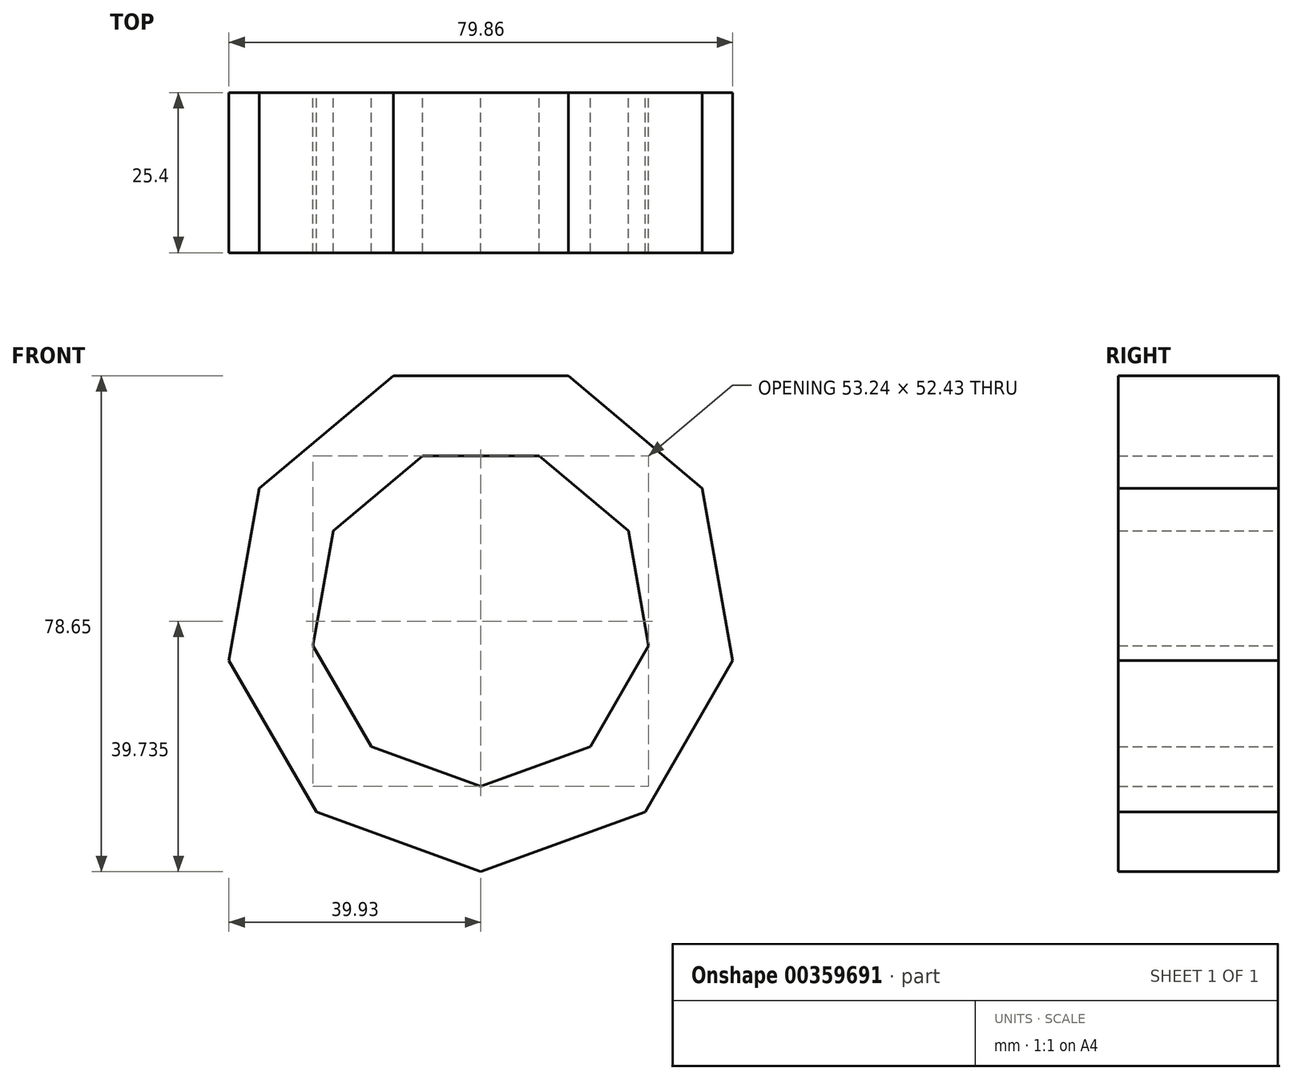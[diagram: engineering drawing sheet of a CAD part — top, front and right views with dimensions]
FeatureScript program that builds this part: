
annotation { "Feature Type Name" : "Feature", "Feature Type Description" : "" }
export const myFeature = defineFeature(function(context is Context, id is Id, definition is map)
    precondition{}
    {
        {
            var Q0;
            Q0=qCreatedBy(makeId("Front.planeOp"),FACE);
            var sketch = newSketch(context, id + "F0", { "sketchPlane" : qUnion([Q0])});
            skLineSegment(sketch, "E0", {"start": v(0, 0) * mm, "end": v(0, 38.1) * mm});
            skCircle(sketch, "E1.cCircle", {"center": v(0, 0) * mm, "radius": 38.1 * mm, "construction": true});
            skLineSegment(sketch, "E1.0", {"start": v(-13.87, 38.1) * mm, "end": v(13.87, 38.1) * mm});
            skLineSegment(sketch, "E1.1", {"start": v(13.87, 38.1) * mm, "end": v(35.11, 20.27) * mm});
            skLineSegment(sketch, "E1.2", {"start": v(35.11, 20.27) * mm, "end": v(39.93, -7.04) * mm});
            skLineSegment(sketch, "E1.3", {"start": v(39.93, -7.04) * mm, "end": v(26.06, -31.06) * mm});
            skLineSegment(sketch, "E1.4", {"start": v(26.06, -31.06) * mm, "end": v(0, -40.55) * mm});
            skLineSegment(sketch, "E1.5", {"start": v(0, -40.55) * mm, "end": v(-26.06, -31.06) * mm});
            skLineSegment(sketch, "E1.6", {"start": v(-26.06, -31.06) * mm, "end": v(-39.93, -7.04) * mm});
            skLineSegment(sketch, "E1.7", {"start": v(-39.93, -7.04) * mm, "end": v(-35.11, 20.27) * mm});
            skLineSegment(sketch, "E1.8", {"start": v(-35.11, 20.27) * mm, "end": v(-13.87, 38.1) * mm});
            skPoint(sketch, "E1.0.midPoint", {"position": v(0, 38.1) * mm});
            skPoint(sketch, "E2.0.midPoint", {"position": v(0, 25.4) * mm});
            skPoint(sketch, "E2.0.start.orphan", {"position": v(-9.24, 25.4) * mm});
            skPoint(sketch, "E2.1.start.orphan", {"position": v(9.24, 25.4) * mm});
            skLineSegment(sketch, "E3", {"start": v(0, 0) * mm, "end": v(0, 19.05) * mm});
            skLineSegment(sketch, "E4", {"start": v(0, 0) * mm, "end": v(0, 25.4) * mm});
            skCircle(sketch, "E5.cCircle", {"center": v(0, 0) * mm, "radius": 25.4 * mm, "construction": true});
            skLineSegment(sketch, "E5.0", {"start": v(-9.24, 25.4) * mm, "end": v(9.24, 25.4) * mm});
            skLineSegment(sketch, "E5.1", {"start": v(9.24, 25.4) * mm, "end": v(23.4, 13.52) * mm});
            skLineSegment(sketch, "E5.2", {"start": v(23.4, 13.52) * mm, "end": v(26.62, -4.7) * mm});
            skLineSegment(sketch, "E5.3", {"start": v(26.62, -4.7) * mm, "end": v(17.37, -20.7) * mm});
            skLineSegment(sketch, "E5.4", {"start": v(17.37, -20.7) * mm, "end": v(0, -27.03) * mm});
            skLineSegment(sketch, "E5.5", {"start": v(0, -27.03) * mm, "end": v(-17.37, -20.7) * mm});
            skLineSegment(sketch, "E5.6", {"start": v(-17.37, -20.7) * mm, "end": v(-26.62, -4.7) * mm});
            skLineSegment(sketch, "E5.7", {"start": v(-26.62, -4.7) * mm, "end": v(-23.4, 13.52) * mm});
            skLineSegment(sketch, "E5.8", {"start": v(-23.4, 13.52) * mm, "end": v(-9.24, 25.4) * mm});
            skSolve(sketch);
        }
        {
            var Q0;
            {var subQ3=sQuery(id+"F0.wireOp",EDGE,"E1.1");Q0=makeQuery(id+"F0.imprint","IMPRINT",FACE,{"disambiguationData":[TD([[makeQuery(id+"F0.imprint","IMPRINT",EDGE,{"derivedFrom":subQ3}),-1.0]])]});}
            extrude(context, id + "F1", {"entities" : qUnion([Q0]), "depth" : 25.4 * mm});
        }
    });
